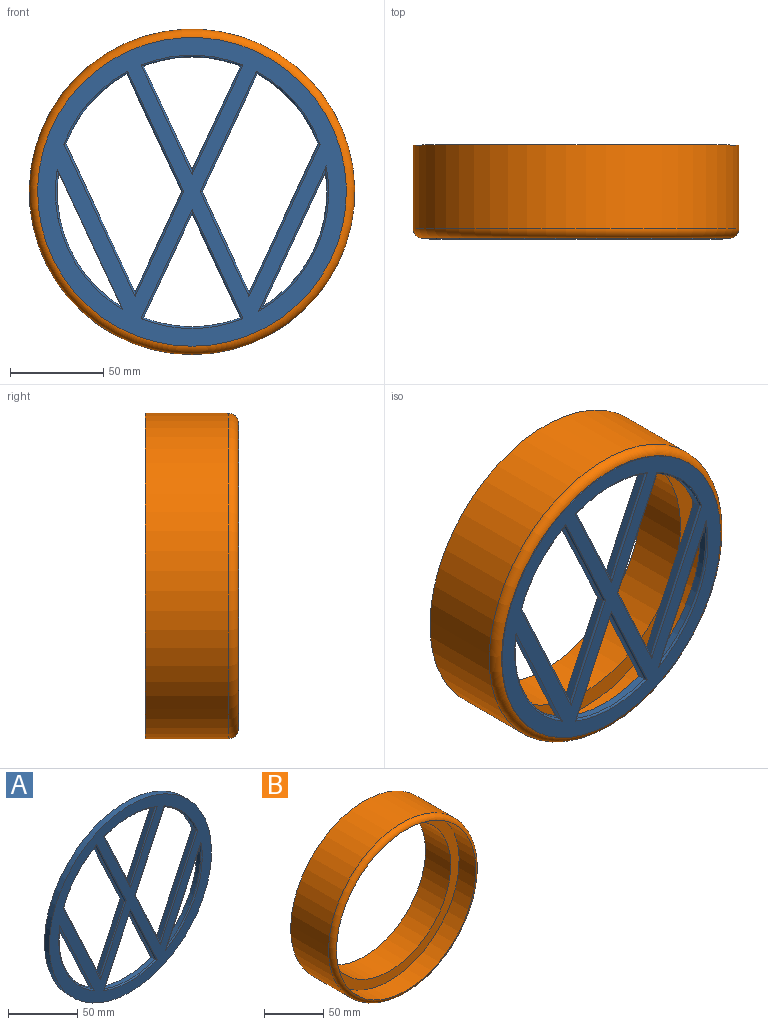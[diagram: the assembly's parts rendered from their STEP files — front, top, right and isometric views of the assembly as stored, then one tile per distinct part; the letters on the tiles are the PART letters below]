
ASSEMBLY  parts=2 mates=1
PART A: 39 faces, bbox 166x5x166 mm
  f0: plane 166x166mm, normal (0,-1,0), area 8451.9mm2, adj f2,f20,f22,f23,f24,f25,f26,f27
  f1: plane 166x166mm, normal (0,1,0), area 9536.2mm2, adj f2,f3,f4,f5,f6,f7,f8,f9
  f2: cylinder r=83mm len=166mm, axis (0,1,0), area 2607.5mm2, adj f0,f1
  f3: plane 63.44x29.58mm, normal (-0.91,0,-0.42), area 280mm2, adj f1,f4,f6,f36
  f4: cylinder r=72.5mm len=37.68mm, axis (0,-1,0), area 203.7mm2, adj f1,f3,f5,f38
  f5: plane 79.63x37.13mm, normal (0.91,0,0.42), area 351.4mm2, adj f1,f4,f6,f37
  f6: plane 53.88x25.12mm, normal (-0.91,0,0.42), area 237.8mm2, adj f1,f3,f5,f35
  f7: cylinder r=72.5mm len=52.07mm, axis (0,-1,0), area 213mm2, adj f1,f8,f9,f23
  f8: plane 55.83x26.04mm, normal (-0.91,0,-0.42), area 246.4mm2, adj f1,f7,f9,f25
  f9: plane 55.83x26.04mm, normal (0.91,0,-0.42), area 246.4mm2, adj f1,f7,f8,f24
  f10: plane 72.31x33.72mm, normal (0.91,0,-0.42), area 319.1mm2, adj f1,f11,f26
  f11: cylinder r=72.5mm len=72.31mm, axis (0,-1,0), area 337.9mm2, adj f1,f10,f27
  f12: cylinder r=72.5mm len=52.07mm, axis (0,-1,0), area 213mm2, adj f1,f13,f14,f32
  f13: plane 55.83x26.04mm, normal (0.91,0,0.42), area 246.4mm2, adj f1,f12,f14,f34
  f14: plane 55.83x26.04mm, normal (-0.91,0,0.42), area 246.4mm2, adj f1,f12,f13,f33
  f15: cylinder r=72.5mm len=37.68mm, axis (0,-1,0), area 203.7mm2, adj f1,f16,f18,f29
  f16: plane 63.44x29.58mm, normal (0.91,0,-0.42), area 280mm2, adj f1,f15,f17,f31
  f17: plane 53.88x25.12mm, normal (0.91,0,0.42), area 237.8mm2, adj f1,f16,f18,f30
  f18: plane 79.63x37.13mm, normal (-0.91,0,0.42), area 351.4mm2, adj f1,f15,f17,f28
  f19: cylinder r=72.5mm len=74.99mm, axis (0,-1,0), area 338.7mm2, adj f1,f20,f21,f22
  f20: plane 75.55x35.23mm, normal (-0.91,0,-0.42), area 319.9mm2, adj f0,f19,f21,f22
  f21: cylinder r=1mm len=75.41mm, axis (-0.42,0,0.91), area 127mm2, adj f1,f19,f20
  f22: torus R=73.5mm, axis (0,-1,0), area 135.1mm2, adj f0,f19,f20
  f23: torus R=73.5mm, axis (0,-1,0), area 85.3mm2, adj f0,f7,f24,f25
  f24: cylinder r=1mm len=59.16mm, axis (0.42,0,0.91), area 98.6mm2, adj f0,f9,f23,f25
  f25: cylinder r=1mm len=59.16mm, axis (0.42,0,-0.91), area 98.6mm2, adj f0,f8,f23,f24
  f26: cylinder r=1mm len=78.54mm, axis (0.42,0,0.91), area 129mm2, adj f0,f10,f27
  f27: torus R=73.5mm, axis (0,-1,0), area 137.1mm2, adj f0,f11,f26
  f28: cylinder r=1mm len=82.38mm, axis (-0.42,0,-0.91), area 139.5mm2, adj f0,f18,f29,f30
  f29: torus R=73.5mm, axis (0,-1,0), area 81.2mm2, adj f0,f15,f28,f31
  f30: cylinder r=1mm len=56.67mm, axis (-0.42,0,0.91), area 94.9mm2, adj f0,f17,f28,f31
  f31: cylinder r=1mm len=65.25mm, axis (0.42,0,0.91), area 110.8mm2, adj f0,f16,f29,f30
  f32: torus R=73.5mm, axis (0,-1,0), area 85.3mm2, adj f0,f12,f33,f34
  f33: cylinder r=1mm len=59.16mm, axis (-0.42,0,-0.91), area 98.6mm2, adj f0,f14,f32,f34
  f34: cylinder r=1mm len=59.16mm, axis (-0.42,0,0.91), area 98.6mm2, adj f0,f13,f32,f33
  f35: cylinder r=1mm len=56.67mm, axis (-0.42,0,-0.91), area 94.9mm2, adj f0,f6,f36,f37
  f36: cylinder r=1mm len=65.25mm, axis (0.42,0,-0.91), area 110.8mm2, adj f0,f3,f35,f38
  f37: cylinder r=1mm len=82.38mm, axis (-0.42,0,0.91), area 139.5mm2, adj f0,f5,f35,f38
  f38: torus R=73.5mm, axis (0,-1,0), area 81.2mm2, adj f0,f4,f36,f37
PART B: 6 faces, bbox 189.4x50x189.4 mm
  f0: cylinder r=73mm len=146mm, axis (0,-1,0), area 13760.2mm2, adj f2,f3
  f1: cylinder r=87.5mm len=175mm, axis (0,1,0), area 24753.8mm2, adj f2,f5
  f2: plane 175x175mm, normal (0,1,0), area 7311.3mm2, adj f0,f1
  f3: plane 166x166mm, normal (0,-1,0), area 4900.9mm2, adj f0,f4
  f4: cylinder r=83mm len=166mm, axis (0,-1,0), area 10430.1mm2, adj f3,f5
  f5: torus R=82.5mm, axis (0,-1,0), area 3967.9mm2, adj f1,f4
PLACE A t=(16.95,-32.04,-3.76)mm
PLACE B t=(16.95,13.41,-3.76)mm
MATE slider A.f2 <-> B.f4  axis (0,-1,0) through (16.95,-37.04,-3.76)mm
